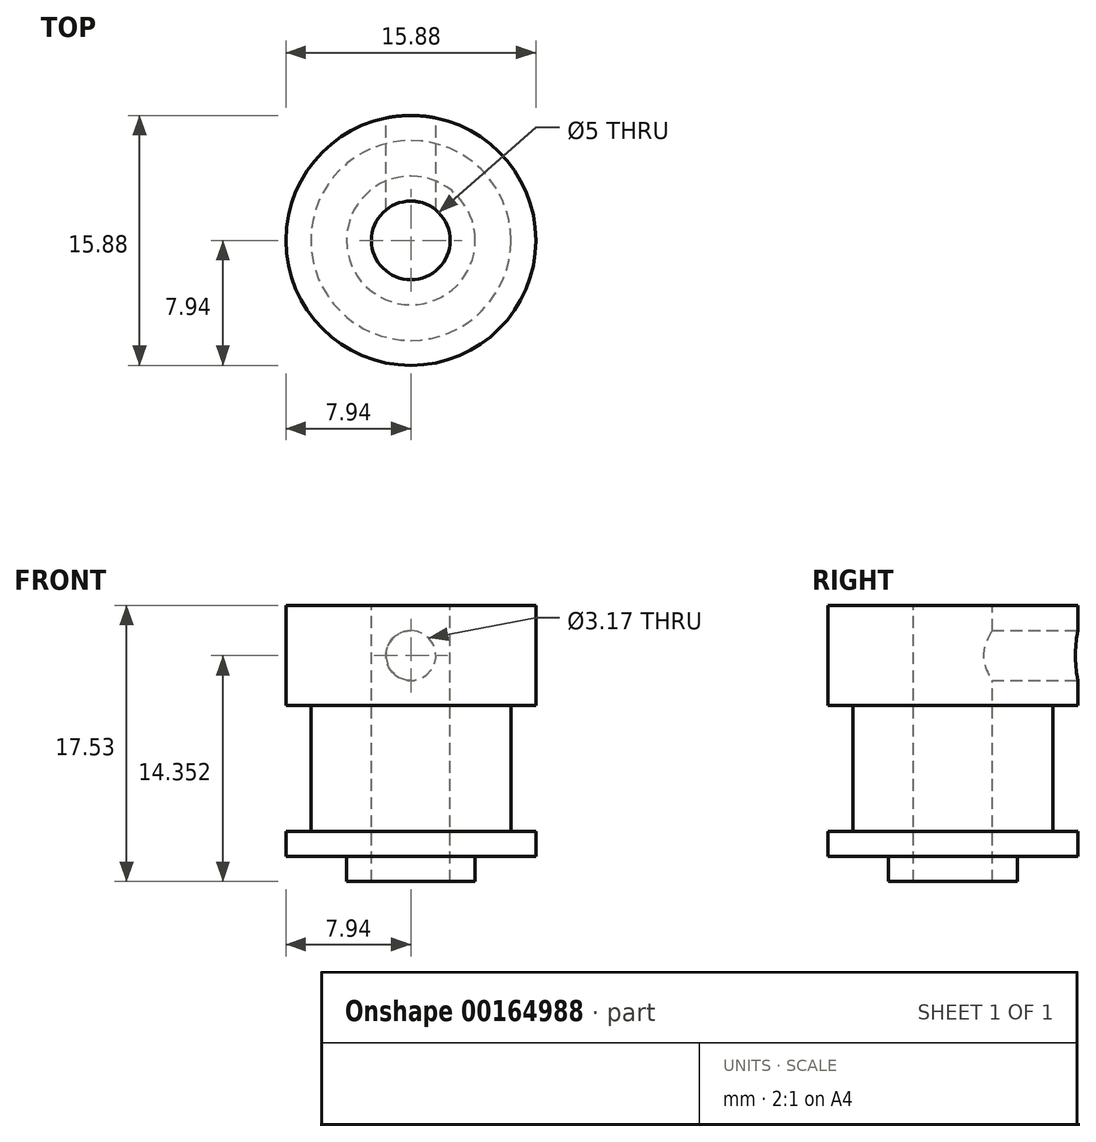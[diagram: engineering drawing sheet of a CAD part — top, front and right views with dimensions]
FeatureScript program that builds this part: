
annotation { "Feature Type Name" : "Feature", "Feature Type Description" : "" }
export const myFeature = defineFeature(function(context is Context, id is Id, definition is map)
    precondition{}
    {
        {
            var Q0;
            Q0=qCreatedBy(makeId("Top.planeOp"),FACE);
            var sketch = newSketch(context, id + "F0", { "sketchPlane" : qUnion([Q0])});
            skCircle(sketch, "E0", {"center": v(0, 0) * mm, "radius": 7.94 * mm});
            skSolve(sketch);
        }
        {
            var Q0;
            Q0=qSketchRegion(id+"F0",true);
            extrude(context, id + "F1", {"entities" : qUnion([Q0]), "depth" : 1.59 * mm});
        }
        {
            var Q0;
            Q0=makeQuery(id+"F1.opExtrude","CAP_FACE",FACE,{"disambiguationData":[OSD([sQuery(id+"F0.wireOp",EDGE,"E0")])],"isStart":false});
            var sketch = newSketch(context, id + "F2", { "sketchPlane" : qUnion([Q0])});
            skCircle(sketch, "E1", {"center": v(0, 0) * mm, "radius": 6.35 * mm});
            skSolve(sketch);
        }
        {
            var Q0;
            Q0=qSketchRegion(id+"F2",true);
            extrude(context, id + "F3", {"entities" : qUnion([Q0]), "operationType" : NewBodyOperationType.ADD, "depth" : 8 * mm});
        }
        {
            var Q0;
            Q0=makeQuery(id+"F3.opExtrude","CAP_FACE",FACE,{"disambiguationData":[OSD([sQuery(id+"F2.wireOp",EDGE,"E1")])],"isStart":false});
            var sketch = newSketch(context, id + "F4", { "sketchPlane" : qUnion([Q0])});
            skCircle(sketch, "E2", {"center": v(0, 0) * mm, "radius": 7.94 * mm, "construction": true});
            skLineSegment(sketch, "E3.bottom", {"start": v(7.94, -7.94) * mm, "end": v(-7.94, -7.94) * mm});
            skLineSegment(sketch, "E3.top", {"start": v(7.94, 7.94) * mm, "end": v(-7.94, 7.94) * mm});
            skLineSegment(sketch, "E3.left", {"start": v(7.94, -7.94) * mm, "end": v(7.94, 7.94) * mm});
            skLineSegment(sketch, "E3.right", {"start": v(-7.94, -7.94) * mm, "end": v(-7.94, 7.94) * mm});
            skSolve(sketch);
        }
        {
            var Q0;
            Q0=qSketchRegion(id+"F4",true);
            extrude(context, id + "F5", {"entities" : qUnion([Q0]), "operationType" : NewBodyOperationType.ADD, "depth" : 6.35 * mm});
        }
        {
            var Q0;
            Q0=makeQuery(id+"F5.opExtrude","CAP_FACE",FACE,{"disambiguationData":[OSD([sQuery(id+"F4.wireOp",EDGE,"E3.bottom"),sQuery(id+"F4.wireOp",EDGE,"E3.top"),sQuery(id+"F4.wireOp",EDGE,"E3.left"),sQuery(id+"F4.wireOp",EDGE,"E3.right")])],"isStart":false});
            var sketch = newSketch(context, id + "F6", { "sketchPlane" : qUnion([Q0])});
            skCircle(sketch, "E4", {"center": v(0, 0) * mm, "radius": 2.5 * mm});
            skSolve(sketch);
        }
        {
            var Q0;
            Q0=qSketchRegion(id+"F6",true);
            var Q1;
            Q1=makeQuery(id+"F1.opExtrude","CAP_FACE",FACE,{"disambiguationData":[OSD([sQuery(id+"F0.wireOp",EDGE,"E0")])],"isStart":true});
            extrude(context, id + "F7", {"entities" : qUnion([Q0]), "operationType" : NewBodyOperationType.REMOVE, "endBound" : BoundingType.UP_TO_SURFACE, "oppositeDirection" : true, "endBoundEntityFace" : qUnion([Q1]), "depth" : 25.4 * mm});
        }
        {
            var Q0;
            Q0=makeQuery(id+"F5.opExtrude","SWEPT_FACE",FACE,{"disambiguationData":[OSD([sQuery(id+"F4.wireOp",EDGE,"E3.top")])]});
            var sketch = newSketch(context, id + "F8", { "sketchPlane" : qUnion([Q0])});
            skLineSegment(sketch, "E5", {"start": v(0, 15.94) * mm, "end": v(0, 9.59) * mm, "construction": true});
            skCircle(sketch, "E6", {"center": v(0, 12.76) * mm, "radius": 1.59 * mm});
            skSolve(sketch);
        }
        {
            var Q0;
            Q0=qSketchRegion(id+"F8",true);
            var Q1;
            Q1=makeQuery(id+"F7.boolean.opBoolean","COPY",FACE,{"derivedFrom":makeQuery(id+"F7.opExtrude","SWEPT_FACE",FACE,{"disambiguationData":[OSD([sQuery(id+"F6.wireOp",EDGE,"E4")])]})});
            extrude(context, id + "F9", {"entities" : qUnion([Q0]), "operationType" : NewBodyOperationType.REMOVE, "endBound" : BoundingType.UP_TO_SURFACE, "oppositeDirection" : true, "endBoundEntityFace" : qUnion([Q1]), "depth" : 25.4 * mm});
        }
        {
            var Q0;
            Q0=makeQuery(id+"F5.opExtrude","SWEPT_EDGE",EDGE,{"disambiguationData":[OSD([sQuery(id+"F4.wireOp",EDGE,"E3.top"),sQuery(id+"F4.wireOp",EDGE,"E3.right")])]});
            var Q1;
            Q1=makeQuery(id+"F5.opExtrude","SWEPT_EDGE",EDGE,{"disambiguationData":[OSD([sQuery(id+"F4.wireOp",EDGE,"E3.bottom"),sQuery(id+"F4.wireOp",EDGE,"E3.right")])]});
            var Q2;
            Q2=makeQuery(id+"F5.opExtrude","SWEPT_EDGE",EDGE,{"disambiguationData":[OSD([sQuery(id+"F4.wireOp",EDGE,"E3.top"),sQuery(id+"F4.wireOp",EDGE,"E3.left")])]});
            var Q3;
            Q3=makeQuery(id+"F5.opExtrude","SWEPT_EDGE",EDGE,{"disambiguationData":[OSD([sQuery(id+"F4.wireOp",EDGE,"E3.bottom"),sQuery(id+"F4.wireOp",EDGE,"E3.left")])]});
            fillet(context, id + "F10", {"entities" : qUnion([Q0, Q1, Q2, Q3]), "radius" : 7.94 * mm, "tangentPropagation" : true, "allowEdgeOverflow" : false});
        }
        {
            var Q0;
            Q0=makeQuery(id+"F1.opExtrude","CAP_FACE",FACE,{"disambiguationData":[OSD([sQuery(id+"F0.wireOp",EDGE,"E0")])],"isStart":true});
            var sketch = newSketch(context, id + "F11", { "sketchPlane" : qUnion([Q0])});
            skCircle(sketch, "E7", {"center": v(0, 0) * mm, "radius": 2.5 * mm});
            skCircle(sketch, "E8", {"center": v(0, 0) * mm, "radius": 4.09 * mm});
            skSolve(sketch);
        }
        {
            var Q0;
            Q0 = qSketchRegion(id + "F11", true);
            extrude(context, id + "F12", {"entities" : qUnion([Q0]), "operationType" : NewBodyOperationType.ADD, "depth" : 1.59 * mm});
        }
    });
